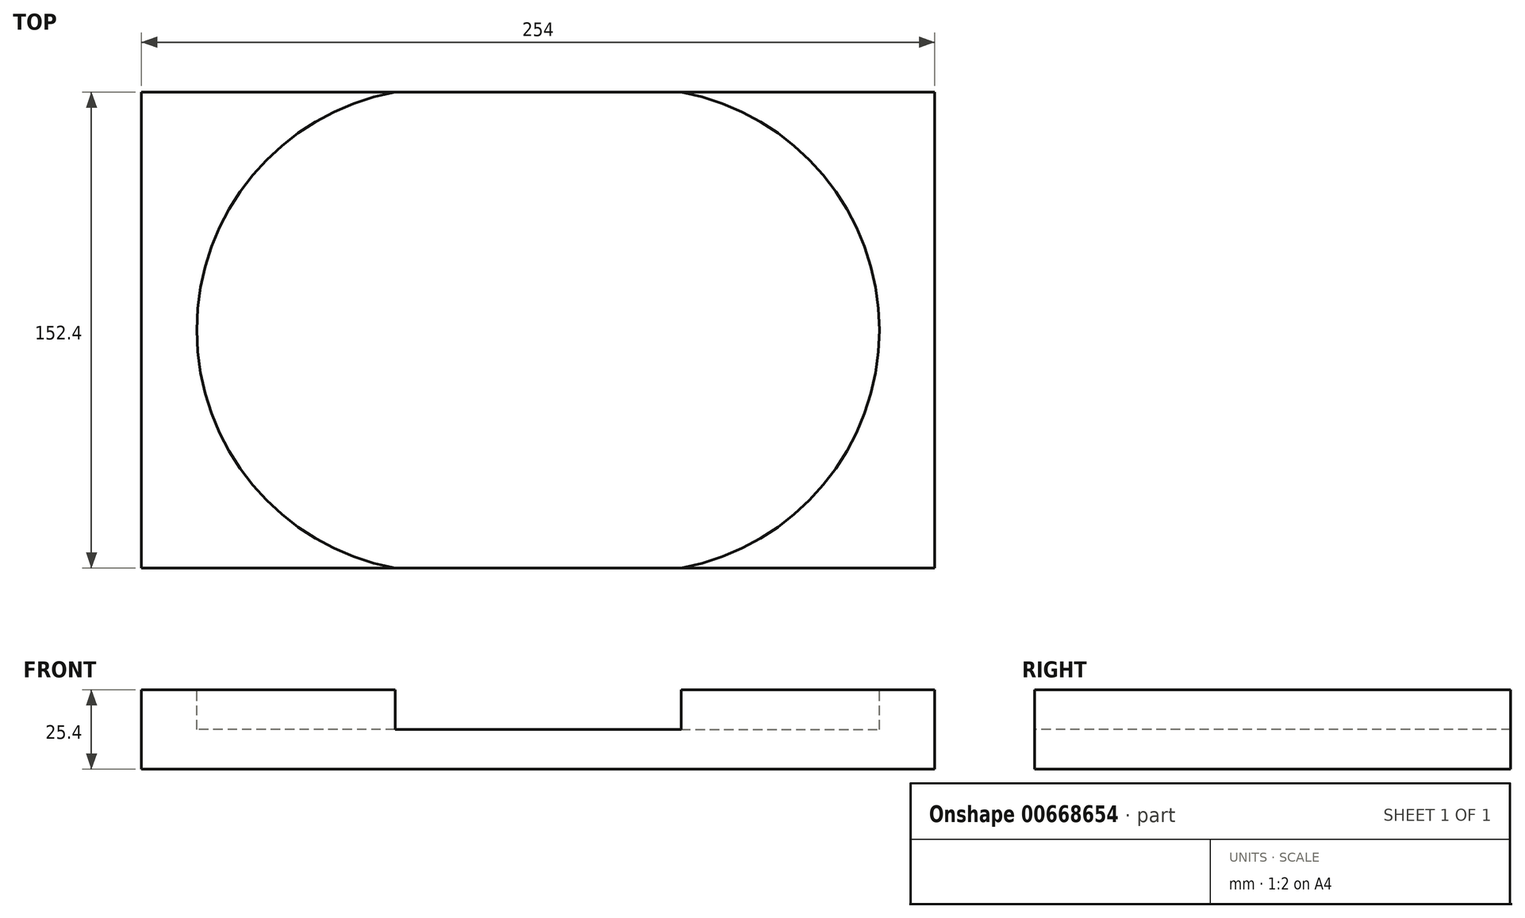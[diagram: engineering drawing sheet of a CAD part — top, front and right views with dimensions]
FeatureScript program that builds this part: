
annotation { "Feature Type Name" : "Feature", "Feature Type Description" : "" }
export const myFeature = defineFeature(function(context is Context, id is Id, definition is map)
    precondition{}
    {
        {
            var Q0;
            Q0=qCreatedBy(makeId("Top.planeOp"),FACE);
            var sketch = newSketch(context, id + "F0", { "sketchPlane" : qUnion([Q0])});
            skLineSegment(sketch, "E0.bottom", {"start": v(-117.44, 91.12) * mm, "end": v(136.56, 91.12) * mm});
            skLineSegment(sketch, "E0.top", {"start": v(-117.44, -61.28) * mm, "end": v(136.56, -61.28) * mm});
            skLineSegment(sketch, "E0.left", {"start": v(-117.44, 91.12) * mm, "end": v(-117.44, -61.28) * mm});
            skLineSegment(sketch, "E0.right", {"start": v(136.56, 91.12) * mm, "end": v(136.56, -61.28) * mm});
            skSolve(sketch);
        }
        {
            var Q0;
            Q0=makeQuery(id+"F0.imprint","IMPRINT",FACE,{"disambiguationData":[TD([[makeQuery(id+"F0.imprint","IMPRINT",EDGE,{"derivedFrom":sQuery(id+"F0.wireOp",EDGE,"E0.bottom")}),-1.0]])]});
            extrude(context, id + "F1", {"entities" : qUnion([Q0]), "depth" : 25.4 * mm, "offsetDistance" : 25.4 * mm});
        }
        {
            var Q0;
            Q0=makeQuery(id+"F1.opExtrude","CAP_FACE",FACE,{"disambiguationData":[OSD([sQuery(id+"F0.wireOp",EDGE,"E0.bottom"),sQuery(id+"F0.wireOp",EDGE,"E0.top"),sQuery(id+"F0.wireOp",EDGE,"E0.left"),sQuery(id+"F0.wireOp",EDGE,"E0.right")])],"isStart":false});
            var sketch = newSketch(context, id + "F2", { "sketchPlane" : qUnion([Q0])});
            skLineSegment(sketch, "E1", {"start": v(9.56, 91.12) * mm, "end": v(9.56, 14.92) * mm});
            skPoint(sketch, "E1.endSnap0", {"position": v(-117.44, 14.92) * mm});
            skLineSegment(sketch, "E2", {"start": v(9.56, 14.92) * mm, "end": v(55.35, -61.28) * mm});
            skLineSegment(sketch, "E3", {"start": v(9.56, 14.92) * mm, "end": v(-36.23, -61.28) * mm});
            skArc(sketch, "E4", {"start": v(-36.23, 91.12) * mm, "mid": v(-99.73, 14.92) * mm, "end": v(-36.23, -61.28) * mm});
            skArc(sketch, "E5", {"start": v(55.35, -61.28) * mm, "mid": v(118.85, 14.92) * mm, "end": v(55.35, 91.12) * mm});
            skSolve(sketch);
        }
        {
            var Q0;
            {var subQ0=sQuery(id+"F2.wireOp",EDGE,"E1");Q0=makeQuery(id+"F2.imprint","IMPRINT",FACE,{"disambiguationData":[TD([[makeQuery(id+"F2.imprint","IMPRINT",EDGE,{"derivedFrom":subQ0}),1.0]])]});}
            var Q1;
            {var subQ0=sQuery(id+"F2.wireOp",EDGE,"E2");Q1=makeQuery(id+"F2.imprint","IMPRINT",FACE,{"disambiguationData":[TD([[makeQuery(id+"F2.imprint","IMPRINT",EDGE,{"derivedFrom":subQ0}),-1.0]])]});}
            var Q2;
            {var subQ0=sQuery(id+"F2.wireOp",EDGE,"E1");Q2=makeQuery(id+"F2.imprint","IMPRINT",FACE,{"disambiguationData":[TD([[makeQuery(id+"F2.imprint","IMPRINT",EDGE,{"derivedFrom":subQ0}),-1.0]])]});}
            extrude(context, id + "F3", {"entities" : qUnion([Q0, Q1, Q2]), "operationType" : NewBodyOperationType.REMOVE, "oppositeDirection" : true, "depth" : 12.7 * mm, "offsetDistance" : 25.4 * mm});
        }
    });
